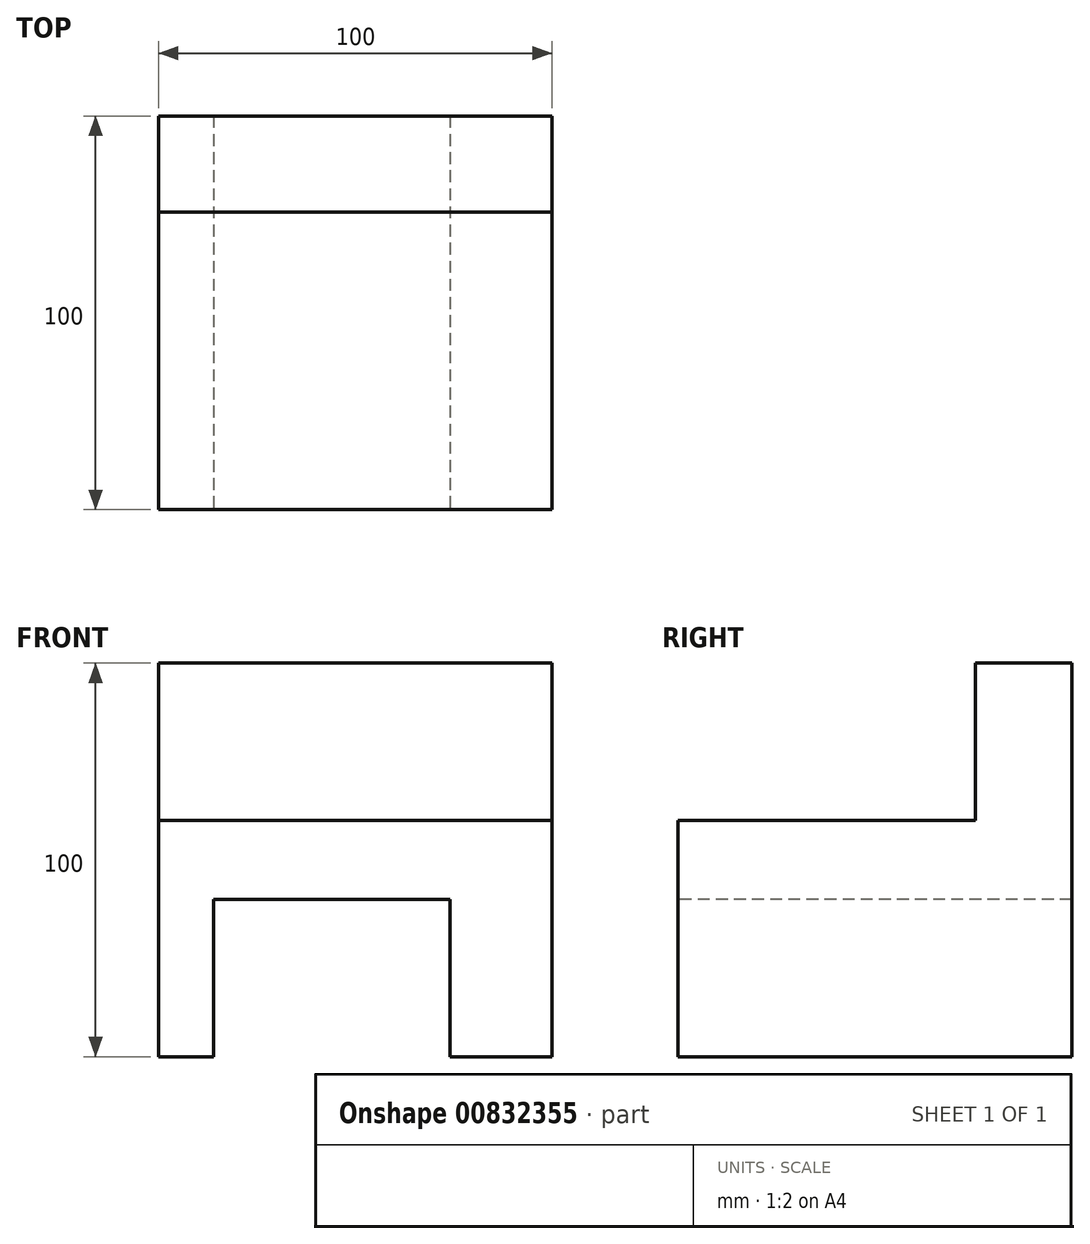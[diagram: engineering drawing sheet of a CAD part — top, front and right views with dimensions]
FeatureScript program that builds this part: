
annotation { "Feature Type Name" : "Feature", "Feature Type Description" : "" }
export const myFeature = defineFeature(function(context is Context, id is Id, definition is map)
    precondition{}
    {
        {
            var Q0;
            Q0=qCreatedBy(makeId("Top.planeOp"),FACE);
            var sketch = newSketch(context, id + "F0", { "sketchPlane" : qUnion([Q0])});
            skLineSegment(sketch, "E0.bottom", {"start": v(50, 50) * mm, "end": v(-50, 50) * mm});
            skLineSegment(sketch, "E0.top", {"start": v(50, -50) * mm, "end": v(-50, -50) * mm});
            skLineSegment(sketch, "E0.left", {"start": v(50, 50) * mm, "end": v(50, -50) * mm});
            skLineSegment(sketch, "E0.right", {"start": v(-50, 50) * mm, "end": v(-50, -50) * mm});
            skPoint(sketch, "E0.middle", {"position": v(0, 0) * mm});
            skSolve(sketch);
        }
        {
            var Q0;
            Q0 = qSketchRegion(id + "F0", true);
            extrude(context, id + "F1", {"entities" : qUnion([Q0]), "depth" : 100 * mm, "offsetDistance" : 25 * mm});
        }
        {
            var Q0;
            Q0=makeQuery(id+"F1.opExtrude","CAP_FACE",FACE,{"disambiguationData":[OSD([sQuery(id+"F0.wireOp",EDGE,"E0.bottom"),sQuery(id+"F0.wireOp",EDGE,"E0.top"),sQuery(id+"F0.wireOp",EDGE,"E0.left"),sQuery(id+"F0.wireOp",EDGE,"E0.right")])],"isStart":false});
            var sketch = newSketch(context, id + "F2", { "sketchPlane" : qUnion([Q0])});
            skLineSegment(sketch, "E1.bottom", {"start": v(-50, -50) * mm, "end": v(50, -50) * mm});
            skLineSegment(sketch, "E1.top", {"start": v(-50, 25.54) * mm, "end": v(50, 25.54) * mm});
            skLineSegment(sketch, "E1.left", {"start": v(-50, -50) * mm, "end": v(-50, 25.54) * mm});
            skLineSegment(sketch, "E1.right", {"start": v(50, -50) * mm, "end": v(50, 25.54) * mm});
            skSolve(sketch);
        }
        {
            var Q0;
            Q0 = qSketchRegion(id + "F2", true);
            extrude(context, id + "F3", {"entities" : qUnion([Q0]), "operationType" : NewBodyOperationType.REMOVE, "oppositeDirection" : true, "depth" : 40 * mm, "offsetDistance" : 25 * mm});
        }
        {
            var Q0;
            Q0=makeQuery(id+"F1.opExtrude","SWEPT_FACE",FACE,{"disambiguationData":[OSD([sQuery(id+"F0.wireOp",EDGE,"E0.top")])]});
            var sketch = newSketch(context, id + "F4", { "sketchPlane" : qUnion([Q0])});
            skLineSegment(sketch, "E2.bottom", {"start": v(-36.02, 0) * mm, "end": v(23.98, 0) * mm});
            skLineSegment(sketch, "E2.top", {"start": v(-36.02, 40) * mm, "end": v(23.98, 40) * mm});
            skLineSegment(sketch, "E2.left", {"start": v(-36.02, 0) * mm, "end": v(-36.02, 40) * mm});
            skLineSegment(sketch, "E2.right", {"start": v(23.98, 0) * mm, "end": v(23.98, 40) * mm});
            skSolve(sketch);
        }
        {
            var Q0;
            Q0=makeQuery(id+"F4.imprint","IMPRINT",FACE,{"disambiguationData":[TD([[makeQuery(id+"F4.imprint","IMPRINT",EDGE,{"derivedFrom":sQuery(id+"F4.wireOp",EDGE,"E2.bottom")}),-1.0]])]});
            extrude(context, id + "F5", {"entities" : qUnion([Q0]), "operationType" : NewBodyOperationType.REMOVE, "endBound" : BoundingType.THROUGH_ALL, "oppositeDirection" : true, "depth" : 25 * mm, "offsetDistance" : 25 * mm});
        }
        {
            var Q0;
            Q0=makeQuery(id+"F4.imprint","IMPRINT",FACE,{"disambiguationData":[TD([[makeQuery(id+"F4.imprint","IMPRINT",EDGE,{"derivedFrom":sQuery(id+"F4.wireOp",EDGE,"E2.bottom")}),-1.0]])]});
            extrude(context, id + "F6", {"entities" : qUnion([Q0]), "operationType" : NewBodyOperationType.REMOVE, "endBound" : BoundingType.THROUGH_ALL, "oppositeDirection" : true, "depth" : 25 * mm, "offsetDistance" : 25 * mm});
        }
    });
